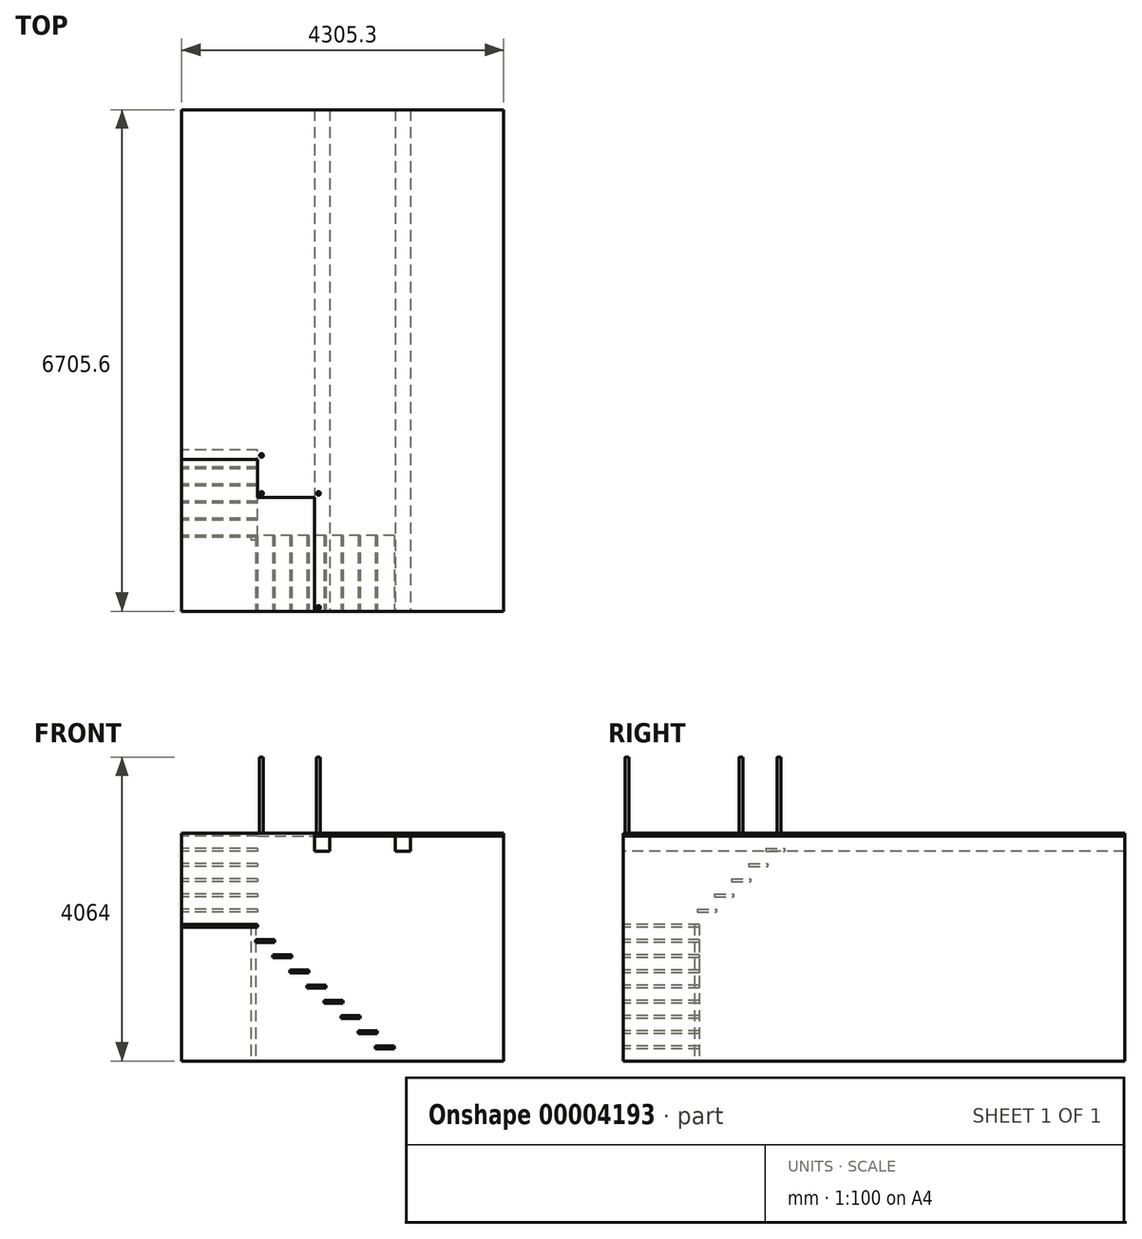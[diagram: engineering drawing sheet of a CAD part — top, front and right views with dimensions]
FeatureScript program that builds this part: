
annotation { "Feature Type Name" : "Feature", "Feature Type Description" : "" }
export const myFeature = defineFeature(function(context is Context, id is Id, definition is map)
    precondition{}
    {
        {
            var Q0;
            Q0=qCreatedBy(makeId("Front.planeOp"),FACE);
            var sketch = newSketch(context, id + "F0", { "sketchPlane" : qUnion([Q0])});
            skLineSegment(sketch, "E0.bottom", {"start": v(1016, 1828.8) * mm, "end": v(0, 1828.8) * mm});
            skLineSegment(sketch, "E0.top", {"start": v(1016, 1790.7) * mm, "end": v(0, 1790.7) * mm});
            skLineSegment(sketch, "E0.left", {"start": v(1016, 1828.8) * mm, "end": v(1016, 1790.7) * mm});
            skLineSegment(sketch, "E0.right", {"start": v(0, 1828.8) * mm, "end": v(0, 1790.7) * mm});
            skLineSegment(sketch, "E1.bottom", {"start": v(1244.6, 1625.6) * mm, "end": v(990.6, 1625.6) * mm});
            skLineSegment(sketch, "E1.top", {"start": v(1244.6, 1587.5) * mm, "end": v(990.6, 1587.5) * mm});
            skLineSegment(sketch, "E1.left", {"start": v(1244.6, 1625.6) * mm, "end": v(1244.6, 1587.5) * mm});
            skLineSegment(sketch, "E1.right", {"start": v(990.6, 1625.6) * mm, "end": v(990.6, 1587.5) * mm});
            skLineSegment(sketch, "E2.bottom", {"start": v(1473.2, 1422.4) * mm, "end": v(1219.2, 1422.4) * mm});
            skLineSegment(sketch, "E2.top", {"start": v(1473.2, 1384.3) * mm, "end": v(1219.2, 1384.3) * mm});
            skLineSegment(sketch, "E2.left", {"start": v(1473.2, 1422.4) * mm, "end": v(1473.2, 1384.3) * mm});
            skLineSegment(sketch, "E2.right", {"start": v(1219.2, 1422.4) * mm, "end": v(1219.2, 1384.3) * mm});
            skLineSegment(sketch, "E3.bottom", {"start": v(1701.8, 1219.2) * mm, "end": v(1447.8, 1219.2) * mm});
            skLineSegment(sketch, "E3.top", {"start": v(1701.8, 1181.1) * mm, "end": v(1447.8, 1181.1) * mm});
            skLineSegment(sketch, "E3.left", {"start": v(1701.8, 1219.2) * mm, "end": v(1701.8, 1181.1) * mm});
            skLineSegment(sketch, "E3.right", {"start": v(1447.8, 1219.2) * mm, "end": v(1447.8, 1181.1) * mm});
            skLineSegment(sketch, "E4.bottom", {"start": v(1930.4, 1016) * mm, "end": v(1676.4, 1016) * mm});
            skLineSegment(sketch, "E4.top", {"start": v(1930.4, 977.9) * mm, "end": v(1676.4, 977.9) * mm});
            skLineSegment(sketch, "E4.left", {"start": v(1930.4, 1016) * mm, "end": v(1930.4, 977.9) * mm});
            skLineSegment(sketch, "E4.right", {"start": v(1676.4, 1016) * mm, "end": v(1676.4, 977.9) * mm});
            skLineSegment(sketch, "E5.bottom", {"start": v(2159, 812.8) * mm, "end": v(1905, 812.8) * mm});
            skLineSegment(sketch, "E5.top", {"start": v(2159, 774.7) * mm, "end": v(1905, 774.7) * mm});
            skLineSegment(sketch, "E5.left", {"start": v(2159, 812.8) * mm, "end": v(2159, 774.7) * mm});
            skLineSegment(sketch, "E5.right", {"start": v(1905, 812.8) * mm, "end": v(1905, 774.7) * mm});
            skLineSegment(sketch, "E6.bottom", {"start": v(2387.6, 609.6) * mm, "end": v(2133.6, 609.6) * mm});
            skLineSegment(sketch, "E6.top", {"start": v(2387.6, 571.5) * mm, "end": v(2133.6, 571.5) * mm});
            skLineSegment(sketch, "E6.left", {"start": v(2387.6, 609.6) * mm, "end": v(2387.6, 571.5) * mm});
            skLineSegment(sketch, "E6.right", {"start": v(2133.6, 609.6) * mm, "end": v(2133.6, 571.5) * mm});
            skLineSegment(sketch, "E7.bottom", {"start": v(2616.2, 406.4) * mm, "end": v(2362.2, 406.4) * mm});
            skLineSegment(sketch, "E7.top", {"start": v(2616.2, 368.3) * mm, "end": v(2362.2, 368.3) * mm});
            skLineSegment(sketch, "E7.left", {"start": v(2616.2, 406.4) * mm, "end": v(2616.2, 368.3) * mm});
            skLineSegment(sketch, "E7.right", {"start": v(2362.2, 406.4) * mm, "end": v(2362.2, 368.3) * mm});
            skLineSegment(sketch, "E8.bottom", {"start": v(2844.8, 203.2) * mm, "end": v(2590.8, 203.2) * mm});
            skLineSegment(sketch, "E8.top", {"start": v(2844.8, 165.1) * mm, "end": v(2590.8, 165.1) * mm});
            skLineSegment(sketch, "E8.left", {"start": v(2844.8, 203.2) * mm, "end": v(2844.8, 165.1) * mm});
            skLineSegment(sketch, "E8.right", {"start": v(2590.8, 203.2) * mm, "end": v(2590.8, 165.1) * mm});
            skLineSegment(sketch, "E9", {"start": v(-74.56, 0) * mm, "end": v(4330, 0) * mm, "construction": true});
            skSolve(sketch);
        }
        {
            var Q0;
            Q0 = qSketchRegion(id + "F0", true);
            extrude(context, id + "F1", {"entities" : qUnion([Q0]), "oppositeDirection" : true, "depth" : 1016 * mm});
        }
        {
            var Q0;
            Q0=qCreatedBy(makeId("Right.planeOp"),FACE);
            var sketch = newSketch(context, id + "F2", { "sketchPlane" : qUnion([Q0])});
            skLineSegment(sketch, "E10.bottom", {"start": v(990.6, 2032) * mm, "end": v(1244.6, 2032) * mm});
            skLineSegment(sketch, "E10.top", {"start": v(990.6, 1993.9) * mm, "end": v(1244.6, 1993.9) * mm});
            skLineSegment(sketch, "E10.left", {"start": v(990.6, 2032) * mm, "end": v(990.6, 1993.9) * mm});
            skLineSegment(sketch, "E10.right", {"start": v(1244.6, 2032) * mm, "end": v(1244.6, 1993.9) * mm});
            skLineSegment(sketch, "E11.bottom", {"start": v(1219.2, 2235.2) * mm, "end": v(1473.2, 2235.2) * mm});
            skLineSegment(sketch, "E11.top", {"start": v(1219.2, 2197.1) * mm, "end": v(1473.2, 2197.1) * mm});
            skLineSegment(sketch, "E11.left", {"start": v(1219.2, 2235.2) * mm, "end": v(1219.2, 2197.1) * mm});
            skLineSegment(sketch, "E11.right", {"start": v(1473.2, 2235.2) * mm, "end": v(1473.2, 2197.1) * mm});
            skLineSegment(sketch, "E12.bottom", {"start": v(1447.8, 2438.4) * mm, "end": v(1701.8, 2438.4) * mm});
            skLineSegment(sketch, "E12.top", {"start": v(1447.8, 2400.3) * mm, "end": v(1701.8, 2400.3) * mm});
            skLineSegment(sketch, "E12.left", {"start": v(1447.8, 2438.4) * mm, "end": v(1447.8, 2400.3) * mm});
            skLineSegment(sketch, "E12.right", {"start": v(1701.8, 2438.4) * mm, "end": v(1701.8, 2400.3) * mm});
            skLineSegment(sketch, "E13.bottom", {"start": v(1676.4, 2641.6) * mm, "end": v(1930.4, 2641.6) * mm});
            skLineSegment(sketch, "E13.top", {"start": v(1676.4, 2603.5) * mm, "end": v(1930.4, 2603.5) * mm});
            skLineSegment(sketch, "E13.left", {"start": v(1676.4, 2641.6) * mm, "end": v(1676.4, 2603.5) * mm});
            skLineSegment(sketch, "E13.right", {"start": v(1930.4, 2641.6) * mm, "end": v(1930.4, 2603.5) * mm});
            skLineSegment(sketch, "E14.bottom", {"start": v(1905, 2844.8) * mm, "end": v(2159, 2844.8) * mm});
            skLineSegment(sketch, "E14.top", {"start": v(1905, 2806.7) * mm, "end": v(2159, 2806.7) * mm});
            skLineSegment(sketch, "E14.left", {"start": v(1905, 2844.8) * mm, "end": v(1905, 2806.7) * mm});
            skLineSegment(sketch, "E14.right", {"start": v(2159, 2844.8) * mm, "end": v(2159, 2806.7) * mm});
            skSolve(sketch);
        }
        {
            var Q0;
            Q0 = qSketchRegion(id + "F2", true);
            extrude(context, id + "F3", {"entities" : qUnion([Q0]), "depth" : 1016 * mm});
        }
        {
            var Q0;
            Q0=qCreatedBy(makeId("Top.planeOp"),FACE);
            var sketch = newSketch(context, id + "F4", { "sketchPlane" : qUnion([Q0])});
            skLineSegment(sketch, "E15.bottom", {"start": v(0, 0) * mm, "end": v(4305.3, 0) * mm});
            skLineSegment(sketch, "E15.top", {"start": v(0, 6705.6) * mm, "end": v(4305.3, 6705.6) * mm});
            skLineSegment(sketch, "E15.left", {"start": v(0, 0) * mm, "end": v(0, 6705.6) * mm});
            skLineSegment(sketch, "E15.right", {"start": v(4305.3, 0) * mm, "end": v(4305.3, 6705.6) * mm});
            skSolve(sketch);
        }
        {
            var Q0;
            Q0 = qSketchRegion(id + "F4", true);
            extrude(context, id + "F5", {"entities" : qUnion([Q0]), "depth" : 3048 * mm});
        }
        {
            var Q0;
            Q0=makeQuery(id+"F5.opExtrude","CAP_FACE",FACE,{"disambiguationData":[OSD([sQuery(id+"F4.wireOp",EDGE,"E15.bottom"),sQuery(id+"F4.wireOp",EDGE,"E15.top"),sQuery(id+"F4.wireOp",EDGE,"E15.left"),sQuery(id+"F4.wireOp",EDGE,"E15.right")])],"isStart":false});
            var sketch = newSketch(context, id + "F6", { "sketchPlane" : qUnion([Q0])});
            skLineSegment(sketch, "E16", {"start": v(1778, 0) * mm, "end": v(1778, 1524) * mm});
            skLineSegment(sketch, "E17", {"start": v(1016, 2032) * mm, "end": v(0, 2032) * mm});
            skLineSegment(sketch, "E18", {"start": v(0, 2032) * mm, "end": v(0, 6705.6) * mm});
            skLineSegment(sketch, "E19", {"start": v(0, 6705.6) * mm, "end": v(4305.3, 6705.6) * mm});
            skLineSegment(sketch, "E20", {"start": v(4305.3, 6705.6) * mm, "end": v(4305.3, 0) * mm});
            skLineSegment(sketch, "E21", {"start": v(4305.3, 0) * mm, "end": v(1778, 0) * mm});
            skLineSegment(sketch, "E22", {"start": v(1016, 2032) * mm, "end": v(1016, 1524) * mm});
            skLineSegment(sketch, "E23", {"start": v(1016, 1524) * mm, "end": v(1778, 1524) * mm});
            skSolve(sketch);
        }
        {
            var Q0;
            Q0 = qSketchRegion(id + "F6", true);
            extrude(context, id + "F7", {"entities" : qUnion([Q0]), "oppositeDirection" : true, "depth" : 38.1 * mm});
        }
        {
            var Q0;
            Q0=makeQuery(id+"F5.opExtrude","CAP_FACE",FACE,{"disambiguationData":[OSD([sQuery(id+"F4.wireOp",EDGE,"E15.bottom"),sQuery(id+"F4.wireOp",EDGE,"E15.top"),sQuery(id+"F4.wireOp",EDGE,"E15.left"),sQuery(id+"F4.wireOp",EDGE,"E15.right")])],"isStart":false});
            var sketch = newSketch(context, id + "F8", { "sketchPlane" : qUnion([Q0])});
            skCircle(sketch, "E24", {"center": v(1066.8, 2082.8) * mm, "radius": 25.4 * mm});
            skCircle(sketch, "E25", {"center": v(1066.8, 1574.8) * mm, "radius": 25.4 * mm});
            skCircle(sketch, "E26", {"center": v(1828.8, 1574.8) * mm, "radius": 25.4 * mm});
            skCircle(sketch, "E27", {"center": v(1828.8, 50.8) * mm, "radius": 25.4 * mm});
            skSolve(sketch);
        }
        {
            var Q0;
            Q0 = qSketchRegion(id + "F8", true);
            extrude(context, id + "F9", {"entities" : qUnion([Q0]), "depth" : 1016 * mm});
        }
        {
            var Q0;
            Q0=makeQuery(id+"F5.opExtrude","SWEPT_FACE",FACE,{"disambiguationData":[OSD([sQuery(id+"F4.wireOp",EDGE,"E15.bottom")])]});
            var sketch = newSketch(context, id + "F10", { "sketchPlane" : qUnion([Q0])});
            skLineSegment(sketch, "E28.bottom", {"start": v(1981.2, 3009.9) * mm, "end": v(1778, 3009.9) * mm});
            skLineSegment(sketch, "E28.top", {"start": v(1981.2, 2806.7) * mm, "end": v(1778, 2806.7) * mm});
            skLineSegment(sketch, "E28.left", {"start": v(1981.2, 3009.9) * mm, "end": v(1981.2, 2806.7) * mm});
            skLineSegment(sketch, "E28.right", {"start": v(1778, 3009.9) * mm, "end": v(1778, 2806.7) * mm});
            skLineSegment(sketch, "E29.bottom", {"start": v(3060.7, 3009.9) * mm, "end": v(2857.5, 3009.9) * mm});
            skLineSegment(sketch, "E29.top", {"start": v(3060.7, 2806.7) * mm, "end": v(2857.5, 2806.7) * mm});
            skLineSegment(sketch, "E29.left", {"start": v(3060.7, 3009.9) * mm, "end": v(3060.7, 2806.7) * mm});
            skLineSegment(sketch, "E29.right", {"start": v(2857.5, 3009.9) * mm, "end": v(2857.5, 2806.7) * mm});
            skSolve(sketch);
        }
        {
            var Q0;
            Q0 = qSketchRegion(id + "F10", true);
            extrude(context, id + "F11", {"entities" : qUnion([Q0]), "oppositeDirection" : true, "depth" : 6705.6 * mm});
        }
        {
            var Q0;
            Q0=makeQuery(id+"F4.imprint","IMPRINT",FACE,{"disambiguationData":[TD([[makeQuery(id+"F4.imprint","IMPRINT",EDGE,{"derivedFrom":sQuery(id+"F4.wireOp",EDGE,"E15.bottom")}),1.0]])]});
            var sketch = newSketch(context, id + "F12", { "sketchPlane" : qUnion([Q0])});
            skLineSegment(sketch, "E30.bottom", {"start": v(990.6, 1016) * mm, "end": v(927.1, 1016) * mm});
            skLineSegment(sketch, "E30.top", {"start": v(990.6, 952.5) * mm, "end": v(927.1, 952.5) * mm});
            skLineSegment(sketch, "E30.left", {"start": v(990.6, 1016) * mm, "end": v(990.6, 952.5) * mm});
            skLineSegment(sketch, "E30.right", {"start": v(927.1, 1016) * mm, "end": v(927.1, 952.5) * mm});
            skSolve(sketch);
        }
        {
            var Q0;
            Q0 = qSketchRegion(id + "F12", true);
            extrude(context, id + "F13", {"entities" : qUnion([Q0]), "depth" : 1828.8 * mm});
        }
    });
